# Revit family: 63_UN_FreeStanding_SPF MINI_Norton
name_source: partatom
category: Lighting Fixtures
units: mm (PartAtom-declared; Revit-internal decimal feet)

## family parameters
Always vertical = Yes
Cut with Voids When Loaded = Yes
Light Source = No
OmniClass Number = 23.80.70.11.14.11
OmniClass Title = Downlights
Part Type = Normal
Room Calculation Point = Yes
Round Connector Dimension = Use Diameter
Shared = No
Work Plane-Based = No

## types (4) — shared parameters
Assembly Code = 63.0
Calc_Symbol_Length = 307 mm  [stored 1.00722 ft]
Calc_Symbol_Width = 160 mm  [stored 0.524934 ft]
Description = IP66 / IK10
Housing_Material = Anthracite
IfcExportAs = IfcLightFixtureType
IfcExportType = USERDEFINED
Lamp = LED
Manufacturer = Norton
Model = SPF
URL = https://www.norton.nl
Voltage = 230 V
Weight = 2,1kg

## per-type parameters (varying)
| type | Apparent Load | Light Source | Luminous Flux (lm) | Wattage Comments |
| SPFMINI83LM1200 | 10 VA | SPF_MINI Geometry : SPFMINI83LM1200 | 1211 lm | 10W |
| SPFMINI83LM2500 | 20 VA | SPF_MINI Geometry : SPFMINI83LM2500 | 2490 lm | 20W |
| SPFMINI84LM2500 | 20 VA | SPF_MINI Geometry : SPFMINI84LM2500 | 2490 lm | 20W |
| SPFMINI84LM1200 | 10 VA | SPF_MINI Geometry : SPFMINI84LM1200 | 1211 lm | 10W |

note: [stored X ft] marks values corroborated as IEEE doubles in the binary element streams (Revit-internal decimal feet)

## geometry (parser evidence)
native form markers: Sweep x10
no freeform markers — native parametric forms only
